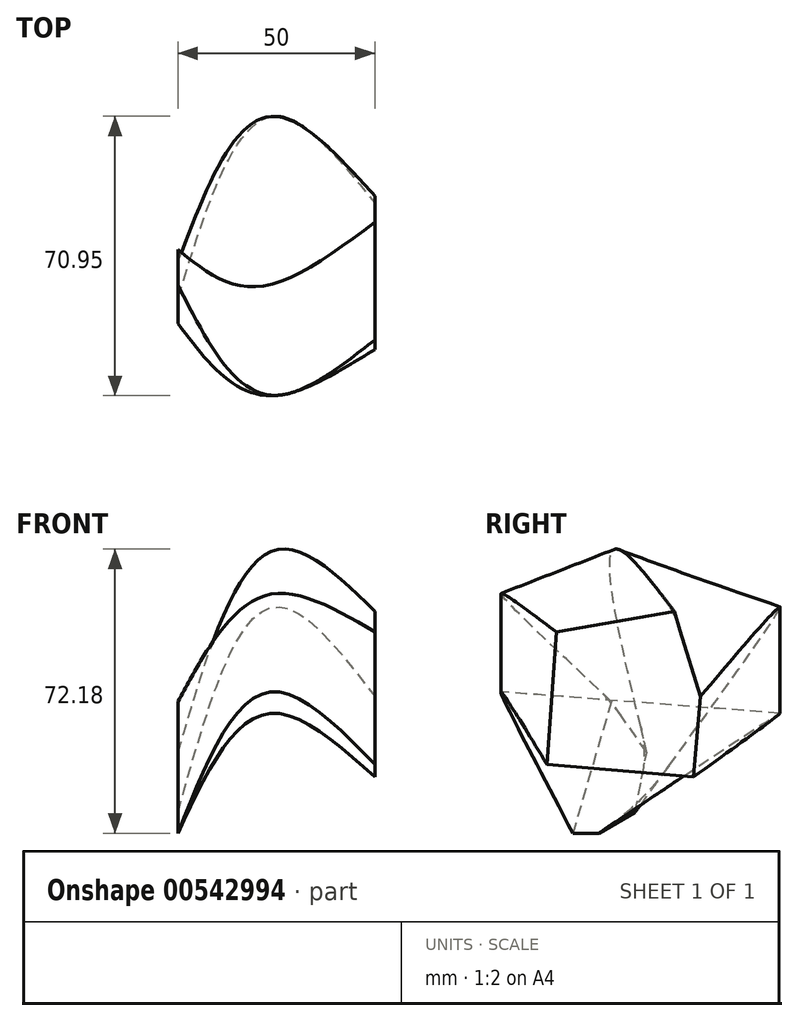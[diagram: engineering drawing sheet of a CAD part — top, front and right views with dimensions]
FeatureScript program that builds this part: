
annotation { "Feature Type Name" : "Feature", "Feature Type Description" : "" }
export const myFeature = defineFeature(function(context is Context, id is Id, definition is map)
    precondition{}
    {
        {
            var Q0;
            Q0=qCreatedBy(makeId("Right.planeOp"),FACE);
            var Q1;
            Q1 = qBodyType(qCreatedBy(id + "F2" ,EDGE), BodyType.WIRE);
            cPlane(context, id + "F0", {"entities" : qUnion([Q0, Q1]), "cplaneType" : CPlaneType.OFFSET, "offset" : 25 * mm, "width" : 150 * mm, "height" : 150 * mm});
        }
        {
            var Q0;
            Q0=qCreatedBy(id+"F0.planeOp",FACE);
            cPlane(context, id + "F1", {"entities" : qUnion([Q0]), "cplaneType" : CPlaneType.OFFSET, "offset" : 25 * mm, "width" : 150 * mm, "height" : 150 * mm});
        }
        {
            var Q0;
            Q0=qCreatedBy(id+"F0.planeOp",FACE);
            var sketch = newSketch(context, id + "F2", { "sketchPlane" : qUnion([Q0])});
            skLineSegment(sketch, "E0", {"start": v(-37.03, -3.38) * mm, "end": v(-37.03, 21.61) * mm});
            skLineSegment(sketch, "E1", {"start": v(-37.03, 21.61) * mm, "end": v(-8.46, 32.7) * mm});
            skLineSegment(sketch, "E2", {"start": v(-8.46, 32.7) * mm, "end": v(33.83, 18.23) * mm});
            skLineSegment(sketch, "E3", {"start": v(33.83, 18.23) * mm, "end": v(33.83, -8.83) * mm});
            skLineSegment(sketch, "E4", {"start": v(33.83, -8.83) * mm, "end": v(-37.03, -3.38) * mm});
            skSolve(sketch);
        }
        {
            var Q0;
            Q0=qCreatedBy(id+"F1.planeOp",FACE);
            var sketch = newSketch(context, id + "F3", { "sketchPlane" : qUnion([Q0])});
            skLineSegment(sketch, "E5", {"start": v(-25.37, -21.8) * mm, "end": v(11.84, -25) * mm});
            skLineSegment(sketch, "E6", {"start": v(11.84, -25) * mm, "end": v(13.6, -4.55) * mm});
            skLineSegment(sketch, "E7", {"start": v(13.6, -4.55) * mm, "end": v(6.95, 17.1) * mm});
            skLineSegment(sketch, "E8", {"start": v(6.95, 17.1) * mm, "end": v(-22.93, 11.84) * mm});
            skLineSegment(sketch, "E9", {"start": v(-22.93, 11.84) * mm, "end": v(-25.37, -21.8) * mm});
            skSolve(sketch);
        }
        {
            var Q0;
            Q0=qCreatedBy(makeId("Right.planeOp"),FACE);
            var sketch = newSketch(context, id + "F4", { "sketchPlane" : qUnion([Q0])});
            skLineSegment(sketch, "E10", {"start": v(-18.8, -39.28) * mm, "end": v(-12.22, -39.28) * mm});
            skLineSegment(sketch, "E11", {"start": v(-12.22, -39.28) * mm, "end": v(-3, -34.02) * mm});
            skLineSegment(sketch, "E12", {"start": v(-3, -34.02) * mm, "end": v(0, -18.8) * mm});
            skLineSegment(sketch, "E13", {"start": v(0, -18.8) * mm, "end": v(-9.02, -5.83) * mm});
            skLineSegment(sketch, "E14", {"start": v(-9.02, -5.83) * mm, "end": v(-18.8, -39.28) * mm});
            skSolve(sketch);
        }
        {
            var Q0;
            Q0 = qSketchRegion(id + "F4", true);
            var Q1;
            Q1 = qSketchRegion(id + "F2", true);
            var Q2;
            Q2 = qSketchRegion(id + "F3", true);
            var Q3;
            Q3 = qConstructionFilter(qBodyType(qCreatedBy(id + "F2" ,EDGE), BodyType.WIRE), ConstructionObject.NO);
            var Q4;
            Q4 = qConstructionFilter(qBodyType(qCreatedBy(id + "F3" ,EDGE), BodyType.WIRE), ConstructionObject.NO);
            var Q5;
            Q5 = qConstructionFilter(qBodyType(qCreatedBy(id + "F4" ,EDGE), BodyType.WIRE), ConstructionObject.NO);
            var Q6;
            Q6=sQuery(id+"F3.wireOp",VERTEX,"E9.start");
            var Q7;
            Q7=sQuery(id+"F2.wireOp",VERTEX,"E0.end");
            var Q8;
            Q8=sQuery(id+"F4.wireOp",VERTEX,"E14.start");
            loft(context, id + "F5", {"sheetProfilesArray" : [{ "sheetProfileEntities" : qUnion([Q0]) }, { "sheetProfileEntities" : qUnion([Q1]) }, { "sheetProfileEntities" : qUnion([Q2]) }], "guidesArray" : [{ "guideEntities" : qUnion([Q3]), "guideDerivativeType" : LoftGuideDerivativeType.DEFAULT, "guideDerivativeMagnitude" : 1 }, { "guideEntities" : qUnion([Q4]), "guideDerivativeType" : LoftGuideDerivativeType.DEFAULT, "guideDerivativeMagnitude" : 1 }, { "guideEntities" : qUnion([Q5]), "guideDerivativeType" : LoftGuideDerivativeType.DEFAULT, "guideDerivativeMagnitude" : 1 }], "matchConnections" : true, "connections" : [{ "connectionEntities" : qUnion([Q6, Q7, Q8]), "connectionEdgeQueries" : qUnion([]), "connectionEdgeParameters" : [] }]});
        }
    });
